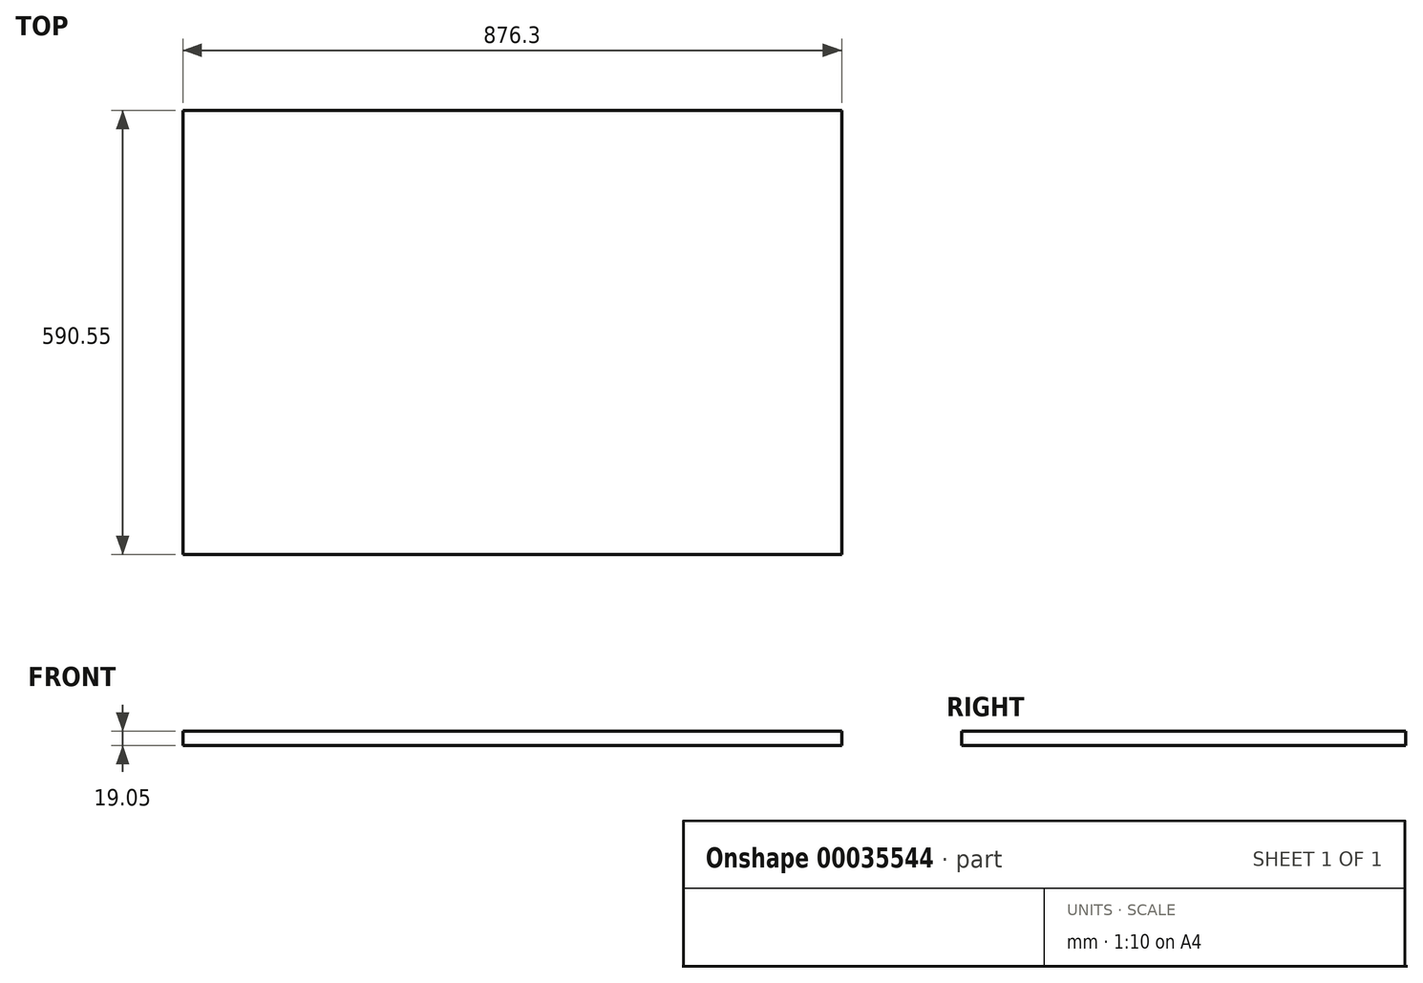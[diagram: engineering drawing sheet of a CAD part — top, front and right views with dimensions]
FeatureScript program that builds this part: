
annotation { "Feature Type Name" : "Feature", "Feature Type Description" : "" }
export const myFeature = defineFeature(function(context is Context, id is Id, definition is map)
    precondition{}
    {
        {
            var Q0;
            Q0=qCreatedBy(makeId("Top.planeOp"),FACE);
            var sketch = newSketch(context, id + "F0", { "sketchPlane" : qUnion([Q0])});
            skLineSegment(sketch, "E0.bottom", {"start": v(-437.16, 318.87) * mm, "end": v(439.14, 318.87) * mm});
            skLineSegment(sketch, "E0.top", {"start": v(-437.16, -271.68) * mm, "end": v(439.14, -271.68) * mm});
            skLineSegment(sketch, "E0.left", {"start": v(-437.16, 318.87) * mm, "end": v(-437.16, -271.68) * mm});
            skLineSegment(sketch, "E0.right", {"start": v(439.14, 318.87) * mm, "end": v(439.14, -271.68) * mm});
            skSolve(sketch);
        }
        {
            var Q0;
            Q0=makeQuery(id+"F0.imprint","IMPRINT",FACE,{"disambiguationData":[TD([[makeQuery(id+"F0.imprint","IMPRINT",EDGE,{"derivedFrom":sQuery(id+"F0.wireOp",EDGE,"E0.bottom")}),-1.0]])]});
            extrude(context, id + "F1", {"entities" : qUnion([Q0]), "depth" : 19.05 * mm});
        }
    });
